# Revit family: QF_ELECTROLUXPROFESSIONAL_1LSNLJ_IC64821FLF_S
name_source: partatom
category: Attrezzature speciali
units: mm (PartAtom-declared; Revit-internal decimal feet)

## family parameters
Basato su piano di lavoro = No
Condiviso = No
Punto di calcolo locali = No
Quota connettore circolare = Usa diametro
Sempre verticale = Sì
Taglio con vuoti quando caricato = No
Tipo di parte = Normale

## types (2) — shared parameters
Depth Actual = 1320 mm
Height Actual = 1460 mm  [stored 4.79003 ft]
Latent Heat Output = 0.0
Length Actual = 2775 mm  [stored 9.10433 ft]
Modello = IC64821FLF
Phase = 3
Produttore = Electrolux Professional
Sensible Heat Output = 0.0
Steam Pounds per Hour = 92
URL = www.electroluxprofessional.com
Volts = 400 V
Watts = 1750 W
Weight = 1100
zero-valued in all types: Gas KW, Prospetto di default

## per-type parameters (varying)
| type | Cycle | Descrizione | Item Number |
| 9882030294 | 50 Hz | IRONER CYLINDER IC64821FLF FEEDING+LENGTH FOLDING 2120MM SUPERIOR STEAM CE 400/50/3 4MM SST CYL. SE, DK, FI VAC.FEED.TAB | 1LM0BG |
| 9882030316 | 60 Hz | IRONER CYLINDER IC64821FLF FEEDING+LENGTH FOLDING 2120MM STEAM CE 400/60/3 4MM SST CYL. ML VAC.FEED.TABLE DIAMMS | 1LT6DB |

note: [stored X ft] marks values corroborated as IEEE doubles in the binary element streams (Revit-internal decimal feet)

## geometry (parser evidence)
native form markers: Sweep x9
no freeform markers — native parametric forms only
